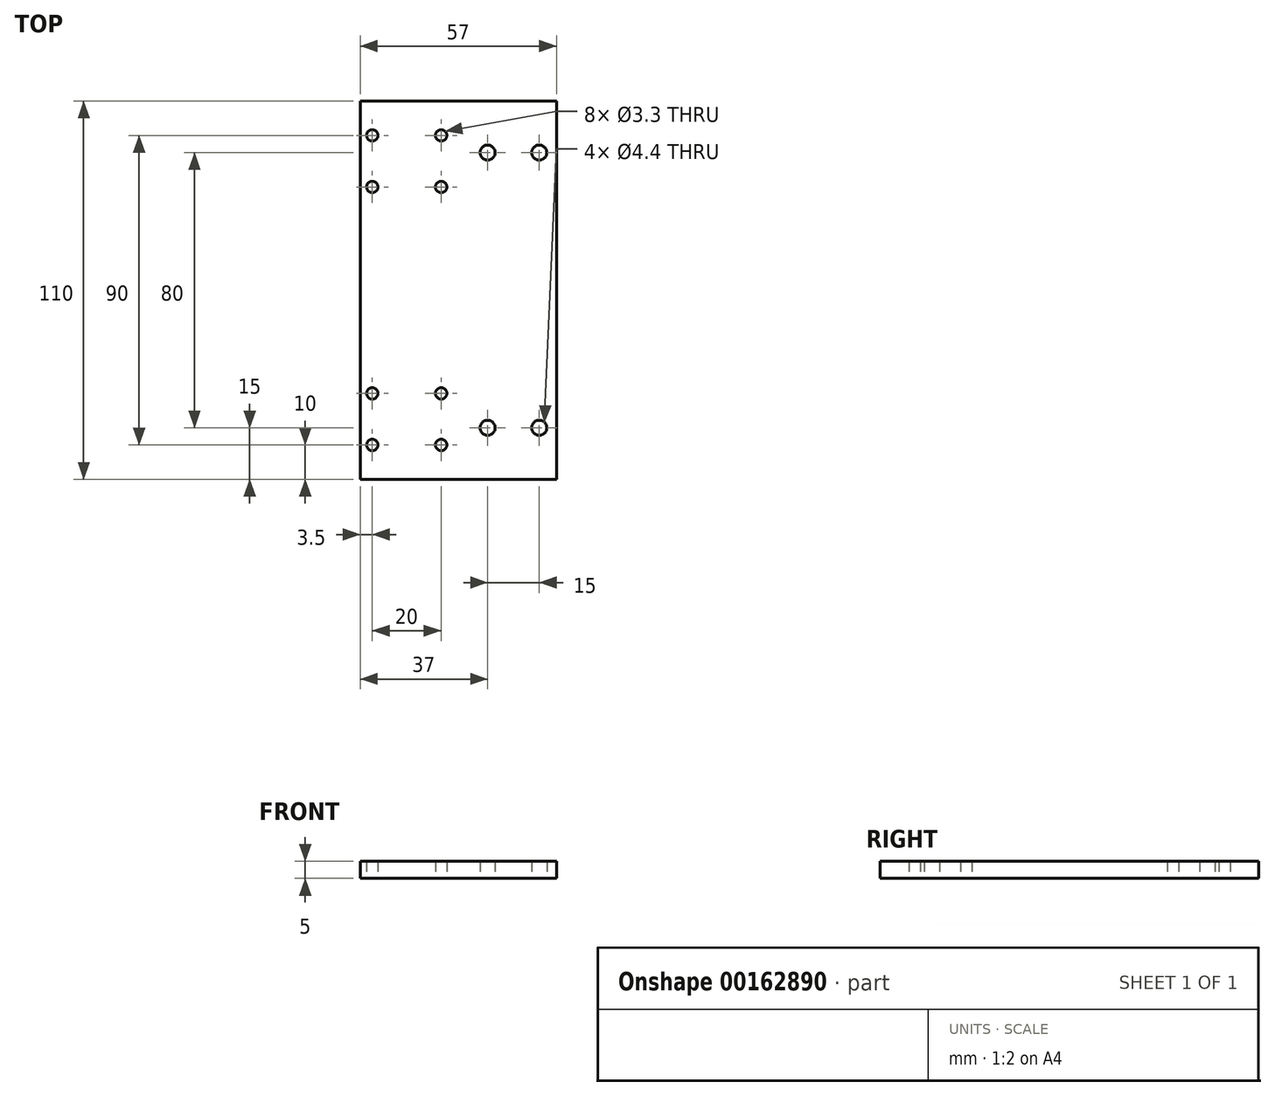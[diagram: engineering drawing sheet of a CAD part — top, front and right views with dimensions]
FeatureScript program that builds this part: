
annotation { "Feature Type Name" : "Feature", "Feature Type Description" : "" }
export const myFeature = defineFeature(function(context is Context, id is Id, definition is map)
    precondition{}
    {
        {
            var Q0;
            Q0=qCreatedBy(makeId("Top.planeOp"),FACE);
            var sketch = newSketch(context, id + "F0", { "sketchPlane" : qUnion([Q0])});
            skPoint(sketch, "E0.middle", {"position": v(0, 0) * mm});
            skLineSegment(sketch, "E1.bottom", {"start": v(-13.5, -55) * mm, "end": v(43.5, -55) * mm});
            skLineSegment(sketch, "E1.top", {"start": v(-13.5, 55) * mm, "end": v(43.5, 55) * mm});
            skLineSegment(sketch, "E1.left", {"start": v(-13.5, -55) * mm, "end": v(-13.5, 55) * mm});
            skLineSegment(sketch, "E1.right", {"start": v(43.5, -55) * mm, "end": v(43.5, 55) * mm});
            skPoint(sketch, "E1.middle", {"position": v(15, 0) * mm});
            skPoint(sketch, "E2", {"position": v(38.5, -40) * mm});
            skPoint(sketch, "E3", {"position": v(23.5, -40) * mm});
            skPoint(sketch, "E4.MirrorP", {"position": v(23.5, 40) * mm});
            skPoint(sketch, "E5.MirrorP", {"position": v(38.5, 40) * mm});
            skLineSegment(sketch, "E6.bottom", {"start": v(10, 30) * mm, "end": v(-10, 30) * mm, "construction": true});
            skLineSegment(sketch, "E6.top", {"start": v(10, 45) * mm, "end": v(-10, 45) * mm, "construction": true});
            skLineSegment(sketch, "E6.left", {"start": v(10, 30) * mm, "end": v(10, 45) * mm, "construction": true});
            skLineSegment(sketch, "E6.right", {"start": v(-10, 30) * mm, "end": v(-10, 45) * mm, "construction": true});
            skPoint(sketch, "E6.middle", {"position": v(0, 37.5) * mm});
            skLineSegment(sketch, "E7.MirrorCS", {"start": v(10, -30) * mm, "end": v(10, -45) * mm, "construction": true});
            skLineSegment(sketch, "E8.MirrorCS", {"start": v(10, -45) * mm, "end": v(-10, -45) * mm, "construction": true});
            skLineSegment(sketch, "E9.MirrorCS", {"start": v(-10, -30) * mm, "end": v(-10, -45) * mm, "construction": true});
            skLineSegment(sketch, "E10.MirrorCS", {"start": v(10, -30) * mm, "end": v(-10, -30) * mm, "construction": true});
            skSolve(sketch);
        }
        {
            var Q0;
            Q0 = qSketchRegion(id + "F0", true);
            extrude(context, id + "F1", {"entities" : qUnion([Q0]), "depth" : 5 * mm, "offsetDistance" : 25 * mm});
        }
        {
            var Q0;
            Q0=sQuery(id+"F0.wireOp",VERTEX,"E6.top.end");
            var Q1;
            Q1=sQuery(id+"F0.wireOp",VERTEX,"E6.bottom.end");
            var Q2;
            Q2=sQuery(id+"F0.wireOp",VERTEX,"E6.bottom.start");
            var Q3;
            Q3=sQuery(id+"F0.wireOp",VERTEX,"E6.top.start");
            var Q4;
            Q4=sQuery(id+"F0.wireOp",VERTEX,"E9.MirrorCS.start");
            var Q5;
            Q5=sQuery(id+"F0.wireOp",VERTEX,"E8.MirrorCS.end");
            var Q6;
            Q6=sQuery(id+"F0.wireOp",VERTEX,"E7.MirrorCS.end");
            var Q7;
            Q7=sQuery(id+"F0.wireOp",VERTEX,"E7.MirrorCS.start");
            var Q8;
            Q8=makeQuery(id+"F1.opExtrude","SWEPT_BODY",BODY,{"disambiguationData":[OSD([sQuery(id+"F0.wireOp",EDGE,"E1.bottom"),sQuery(id+"F0.wireOp",EDGE,"E1.top"),sQuery(id+"F0.wireOp",EDGE,"E1.left"),sQuery(id+"F0.wireOp",EDGE,"E1.right")])]});
            hole(context, id + "F2", {"style" : HoleStyle.SIMPLE, "endStyle" : HoleEndStyle.THROUGH, "oppositeDirection" : true, "standardTappedOrClearance" : lookupTablePath({ "standard" : "ISO", "fit" : "Normal", "size" : "M3", "type" : "Clearance" }), "standardBlindInLast" : lookupTablePath({ "fit" : "Standard", "standard" : "ISO", "size" : "M3", "type" : "Clearance" }), "holeDiameter" : 3.3 * mm, "majorDiameter" : 3 * mm, "isTappedThrough" : true, "tappedDepth" : 12 * mm, "tapClearance" : 3, "startFromSketch" : true, "locations" : qUnion([Q0, Q1, Q2, Q3, Q4, Q5, Q6, Q7]), "scope" : qUnion([Q8])});
        }
        {
            var Q0;
            Q0=sQuery(id+"F0.wireOp",VERTEX,"E4.MirrorP");
            var Q1;
            Q1=sQuery(id+"F0.wireOp",VERTEX,"E5.MirrorP");
            var Q2;
            Q2=sQuery(id+"F0.wireOp",VERTEX,"E3");
            var Q3;
            Q3=sQuery(id+"F0.wireOp",VERTEX,"E2");
            var Q4;
            Q4=makeQuery(id+"F1.opExtrude","SWEPT_BODY",BODY,{"disambiguationData":[OSD([sQuery(id+"F0.wireOp",EDGE,"E1.bottom"),sQuery(id+"F0.wireOp",EDGE,"E1.top"),sQuery(id+"F0.wireOp",EDGE,"E1.left"),sQuery(id+"F0.wireOp",EDGE,"E1.right")])]});
            hole(context, id + "F3", {"style" : HoleStyle.SIMPLE, "endStyle" : HoleEndStyle.THROUGH, "oppositeDirection" : true, "standardTappedOrClearance" : lookupTablePath({ "standard" : "ISO", "fit" : "Normal", "size" : "M4", "type" : "Clearance" }), "standardBlindInLast" : lookupTablePath({ "fit" : "Standard", "standard" : "ISO", "size" : "M4", "type" : "Clearance" }), "holeDiameter" : 4.4 * mm, "majorDiameter" : 3 * mm, "isTappedThrough" : true, "tappedDepth" : 12 * mm, "tapClearance" : 3, "startFromSketch" : true, "locations" : qUnion([Q0, Q1, Q2, Q3]), "scope" : qUnion([Q4])});
        }
    });
